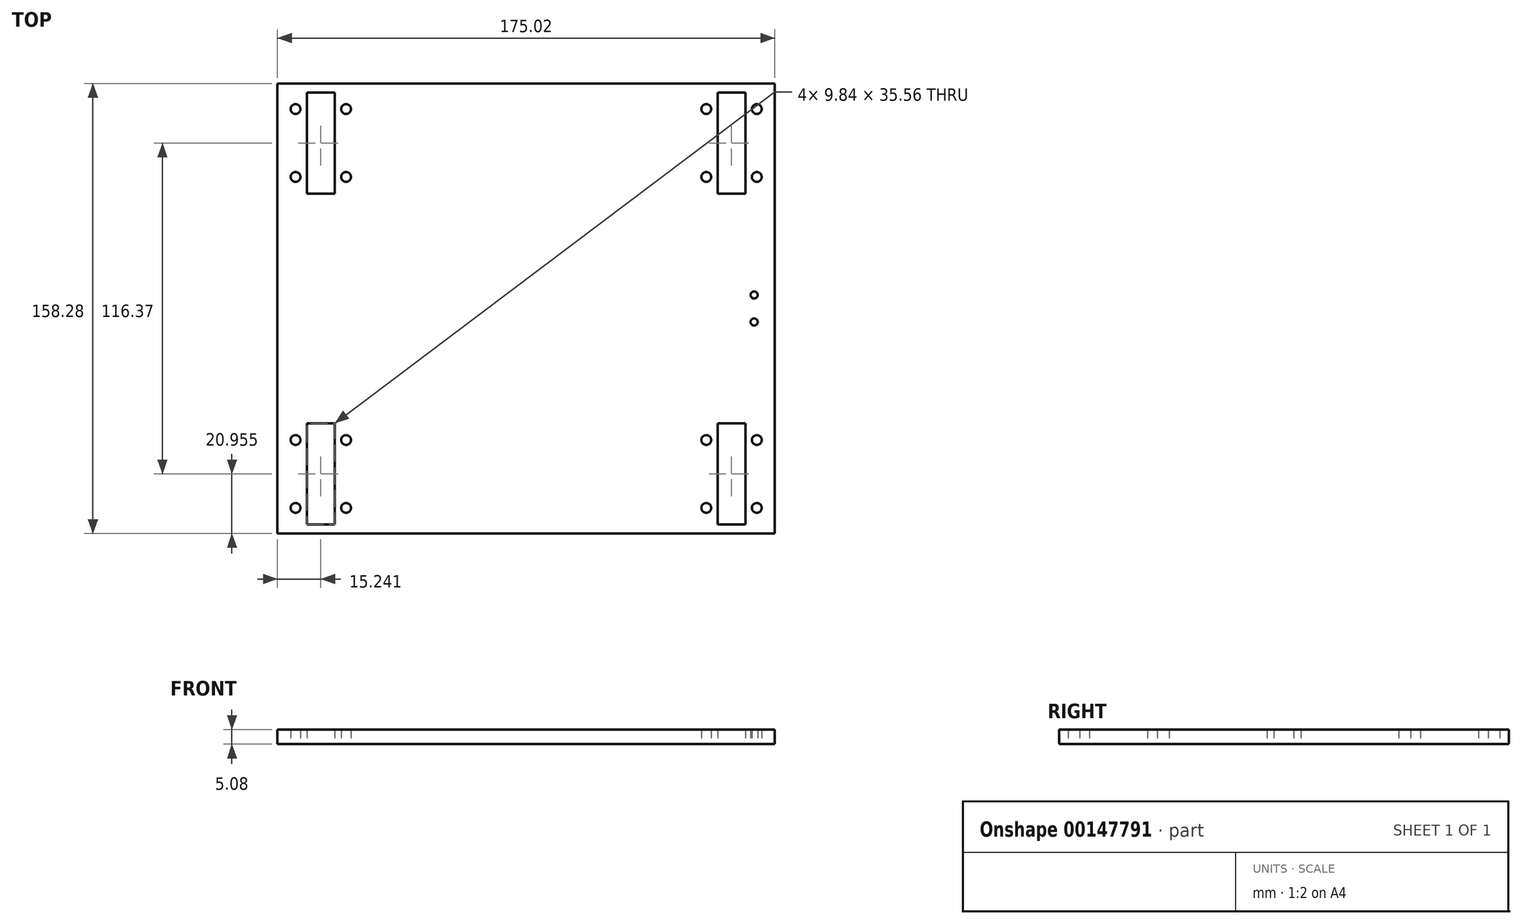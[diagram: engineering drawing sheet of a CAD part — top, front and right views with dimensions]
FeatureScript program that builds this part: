
annotation { "Feature Type Name" : "Feature", "Feature Type Description" : "" }
export const myFeature = defineFeature(function(context is Context, id is Id, definition is map)
    precondition{}
    {
        {
            var Q0;
            Q0=qCreatedBy(makeId("Top.planeOp"),FACE);
            var sketch = newSketch(context, id + "F0", { "sketchPlane" : qUnion([Q0])});
            skLineSegment(sketch, "E0.bottom", {"start": v(87.5, -79.14) * mm, "end": v(-87.5, -79.14) * mm});
            skLineSegment(sketch, "E0.top", {"start": v(87.5, 79.14) * mm, "end": v(-87.5, 79.14) * mm});
            skLineSegment(sketch, "E0.left", {"start": v(87.5, -79.14) * mm, "end": v(87.5, 79.14) * mm});
            skLineSegment(sketch, "E0.right", {"start": v(-87.5, -79.14) * mm, "end": v(-87.5, 79.14) * mm});
            skPoint(sketch, "E0.middle", {"position": v(0, 0) * mm});
            skLineSegment(sketch, "E1", {"start": v(-81.16, 79.14) * mm, "end": v(-81.16, 70.12) * mm, "construction": true});
            skLineSegment(sketch, "E2", {"start": v(-81.16, 70.12) * mm, "end": v(-87.5, 70.12) * mm, "construction": true});
            skLineSegment(sketch, "E3.bottom", {"start": v(-72.27, 58.19) * mm, "end": v(72.27, 58.19) * mm, "construction": true});
            skLineSegment(sketch, "E3.top", {"start": v(-72.27, -58.19) * mm, "end": v(72.27, -58.19) * mm, "construction": true});
            skLineSegment(sketch, "E3.left", {"start": v(-72.27, 58.19) * mm, "end": v(-72.27, -58.19) * mm, "construction": true});
            skLineSegment(sketch, "E3.right", {"start": v(72.27, 58.19) * mm, "end": v(72.27, -58.19) * mm, "construction": true});
            skLineSegment(sketch, "E4.bottom", {"start": v(-81.16, 70.12) * mm, "end": v(-63.38, 70.12) * mm, "construction": true});
            skLineSegment(sketch, "E4.top", {"start": v(-81.16, 46.25) * mm, "end": v(-63.38, 46.25) * mm, "construction": true});
            skLineSegment(sketch, "E4.left", {"start": v(-81.16, 70.12) * mm, "end": v(-81.16, 46.25) * mm, "construction": true});
            skLineSegment(sketch, "E4.right", {"start": v(-63.38, 70.12) * mm, "end": v(-63.38, 46.25) * mm, "construction": true});
            skPoint(sketch, "E4.middle", {"position": v(-72.27, 58.19) * mm});
            skLineSegment(sketch, "E5.bottom", {"start": v(81.16, 70.12) * mm, "end": v(63.38, 70.12) * mm, "construction": true});
            skLineSegment(sketch, "E5.top", {"start": v(81.16, 46.25) * mm, "end": v(63.38, 46.25) * mm, "construction": true});
            skLineSegment(sketch, "E5.left", {"start": v(81.16, 70.12) * mm, "end": v(81.16, 46.25) * mm, "construction": true});
            skLineSegment(sketch, "E5.right", {"start": v(63.38, 70.12) * mm, "end": v(63.38, 46.25) * mm, "construction": true});
            skPoint(sketch, "E5.middle", {"position": v(72.27, 58.19) * mm});
            skLineSegment(sketch, "E6.bottom", {"start": v(81.16, -70.12) * mm, "end": v(63.38, -70.12) * mm, "construction": true});
            skLineSegment(sketch, "E6.top", {"start": v(81.16, -46.25) * mm, "end": v(63.38, -46.25) * mm, "construction": true});
            skLineSegment(sketch, "E6.left", {"start": v(81.16, -70.12) * mm, "end": v(81.16, -46.25) * mm, "construction": true});
            skLineSegment(sketch, "E6.right", {"start": v(63.38, -70.12) * mm, "end": v(63.38, -46.25) * mm, "construction": true});
            skPoint(sketch, "E6.middle", {"position": v(72.27, -58.19) * mm});
            skLineSegment(sketch, "E7.bottom", {"start": v(-63.38, -70.12) * mm, "end": v(-81.16, -70.12) * mm, "construction": true});
            skLineSegment(sketch, "E7.top", {"start": v(-63.38, -46.25) * mm, "end": v(-81.16, -46.25) * mm, "construction": true});
            skLineSegment(sketch, "E7.left", {"start": v(-63.38, -70.12) * mm, "end": v(-63.38, -46.25) * mm, "construction": true});
            skLineSegment(sketch, "E7.right", {"start": v(-81.16, -70.12) * mm, "end": v(-81.16, -46.25) * mm, "construction": true});
            skPoint(sketch, "E7.middle", {"position": v(-72.27, -58.19) * mm});
            skCircle(sketch, "E8", {"center": v(-81.16, 70.12) * mm, "radius": 1.73 * mm});
            skCircle(sketch, "E9", {"center": v(-63.38, 70.12) * mm, "radius": 1.73 * mm});
            skCircle(sketch, "E10", {"center": v(-63.38, 46.25) * mm, "radius": 1.73 * mm});
            skCircle(sketch, "E11", {"center": v(-81.16, 46.25) * mm, "radius": 1.73 * mm});
            skCircle(sketch, "E12", {"center": v(81.16, 46.25) * mm, "radius": 1.73 * mm});
            skCircle(sketch, "E13", {"center": v(81.16, 70.12) * mm, "radius": 1.73 * mm});
            skCircle(sketch, "E14", {"center": v(63.38, 70.12) * mm, "radius": 1.73 * mm});
            skCircle(sketch, "E15", {"center": v(63.38, 46.25) * mm, "radius": 1.73 * mm});
            skCircle(sketch, "E16", {"center": v(81.16, -70.12) * mm, "radius": 1.73 * mm});
            skCircle(sketch, "E17", {"center": v(81.16, -46.25) * mm, "radius": 1.73 * mm});
            skCircle(sketch, "E18", {"center": v(63.38, -46.25) * mm, "radius": 1.73 * mm});
            skCircle(sketch, "E19", {"center": v(63.38, -70.12) * mm, "radius": 1.73 * mm});
            skCircle(sketch, "E20", {"center": v(-63.38, -70.12) * mm, "radius": 1.73 * mm});
            skCircle(sketch, "E21", {"center": v(-63.38, -46.25) * mm, "radius": 1.73 * mm});
            skCircle(sketch, "E22", {"center": v(-81.16, -46.25) * mm, "radius": 1.73 * mm});
            skCircle(sketch, "E23", {"center": v(-81.16, -70.12) * mm, "radius": 1.73 * mm});
            skLineSegment(sketch, "E24", {"start": v(87.5, 0) * mm, "end": v(80.2, 0) * mm, "construction": true});
            skLineSegment(sketch, "E25", {"start": v(80.2, 4.75) * mm, "end": v(80.2, -4.75) * mm, "construction": true});
            skCircle(sketch, "E26", {"center": v(80.2, 4.75) * mm, "radius": 1.25 * mm});
            skCircle(sketch, "E27", {"center": v(80.2, -4.75) * mm, "radius": 1.25 * mm});
            skLineSegment(sketch, "E28.bottom", {"start": v(-67.35, -75.97) * mm, "end": v(-77.19, -75.97) * mm});
            skLineSegment(sketch, "E28.top", {"start": v(-67.35, -40.4) * mm, "end": v(-77.19, -40.4) * mm});
            skLineSegment(sketch, "E28.left", {"start": v(-67.35, -75.97) * mm, "end": v(-67.35, -40.4) * mm});
            skLineSegment(sketch, "E28.right", {"start": v(-77.19, -75.97) * mm, "end": v(-77.19, -40.4) * mm});
            skLineSegment(sketch, "E29.bottom", {"start": v(77.19, -75.97) * mm, "end": v(67.35, -75.97) * mm});
            skLineSegment(sketch, "E29.top", {"start": v(77.19, -40.4) * mm, "end": v(67.35, -40.4) * mm});
            skLineSegment(sketch, "E29.left", {"start": v(77.19, -75.97) * mm, "end": v(77.19, -40.4) * mm});
            skLineSegment(sketch, "E29.right", {"start": v(67.35, -75.97) * mm, "end": v(67.35, -40.4) * mm});
            skLineSegment(sketch, "E30.bottom", {"start": v(77.19, 75.97) * mm, "end": v(67.35, 75.97) * mm});
            skLineSegment(sketch, "E30.top", {"start": v(77.19, 40.4) * mm, "end": v(67.35, 40.4) * mm});
            skLineSegment(sketch, "E30.left", {"start": v(77.19, 75.97) * mm, "end": v(77.19, 40.4) * mm});
            skLineSegment(sketch, "E30.right", {"start": v(67.35, 75.97) * mm, "end": v(67.35, 40.4) * mm});
            skLineSegment(sketch, "E31.bottom", {"start": v(-67.35, 40.4) * mm, "end": v(-77.19, 40.4) * mm});
            skLineSegment(sketch, "E31.top", {"start": v(-67.35, 75.97) * mm, "end": v(-77.19, 75.97) * mm});
            skLineSegment(sketch, "E31.left", {"start": v(-67.35, 40.4) * mm, "end": v(-67.35, 75.97) * mm});
            skLineSegment(sketch, "E31.right", {"start": v(-77.19, 40.4) * mm, "end": v(-77.19, 75.97) * mm});
            skLineSegment(sketch, "E32", {"start": v(-72.27, -75.97) * mm, "end": v(-72.27, -79.14) * mm, "construction": true});
            skLineSegment(sketch, "E33", {"start": v(-67.35, -75.97) * mm, "end": v(-63.38, -75.97) * mm, "construction": true});
            skLineSegment(sketch, "E34", {"start": v(-63.38, -75.97) * mm, "end": v(-63.38, -70.12) * mm, "construction": true});
            skSolve(sketch);
        }
        {
            var Q0;
            Q0=qSketchRegion(id+"F0",true);
            extrude(context, id + "F1", {"entities" : qUnion([Q0]), "depth" : 5.08 * mm});
        }
    });
